# Revit family: Window-Awning-All_Weather-Series_6000
name_source: partatom
category: Windows
units: mm (PartAtom-declared; Revit-internal decimal feet)

## family parameters
Always vertical = Yes
Classification Number = 23.30.20.00
Cut with Voids When Loaded = No
Host = Wall
Room Calculation Point = No
Shared = No

## types (2) — shared parameters
Analytic Construction = <None>
Assembly Code = B2020100
Default Sill Height = 3' - 0"
Description = 2 1/2 in Thermal Break Aluminum Windows
Finish = Metal-Aluminum-All_Weather-Standard-White
Glass = Glass-All_Weather-OA-Insulated_Glass
Glass Thickness = 0' - 1"
Grille = No
Grille Size = 0' - 2 1/2"
Height = 3' - 0"
Horizontal Grille Length = 2' - 6"
Horizontal Grille Offset = 0' - 9 5/8"
Horizontal Grille Spacing = 0' - 10 7/8"
Horizontal Mullions = 2
Inset = 0' - 0"
Jamb Ext Finish = Metal-Aluminum-All_Weather-Standard-White
Jamb Extensions = No
Lites High = 2
Lites Wide = 2
Manufacturer = All Weather Architectural Aluminum
Max Height = 3' - 0"
Max Width = 6' - 0"
Min Height = 1' - 2"
Min Width = 1' - 2"
Model = Awning
Nail Fin Offset = 0' - 1"
Offset = 0' - 0"
Operation = Vent
Product Documentation Link = https://28a25771709x0a343azkftap-wpengine.netdna-ssl.com
Product Name = Series 6000
Product Page URL = https://www.allweatheraa.com
Requested Height = 3' - 0"
Requested Width = 3' - 0"
Rough Height = 3' - 0 3/4"
Rough Width = 3' - 0 3/4"
Specification = https://28a25771709x0a343azkftap-wpengine.netdna-ssl.com
Traditional Grille Horizontal Array = No
Traditional Grille Horizontal Single = No
Traditional Grille Vertical Array = No
Traditional Grille Vertical Single = No
URL = https://www.allweatheraa.com
Vertical Grille Length = 2' - 6"
Vertical Grille Offset = 0' - 9 5/8"
Vertical Grille Spacing = 0' - 10 7/8"
Vertical Mullions = 2
Wall Closure = By host
Warranty = https://www.allweatheraa.com
Width = 3' - 0"

## per-type parameters (varying)
| type | Nail On Frame | Panning Frame | Thickness | Type Comments |
| Nail On Frame Awning | Yes | No | 0' - 3 1/2" | Standard Nail On Frame |
| Panning Frame Awning | No | Yes | 0' - 5" | Panning Frame |

## geometry (parser evidence)
native form markers: Sweep x7
no freeform markers — native parametric forms only
